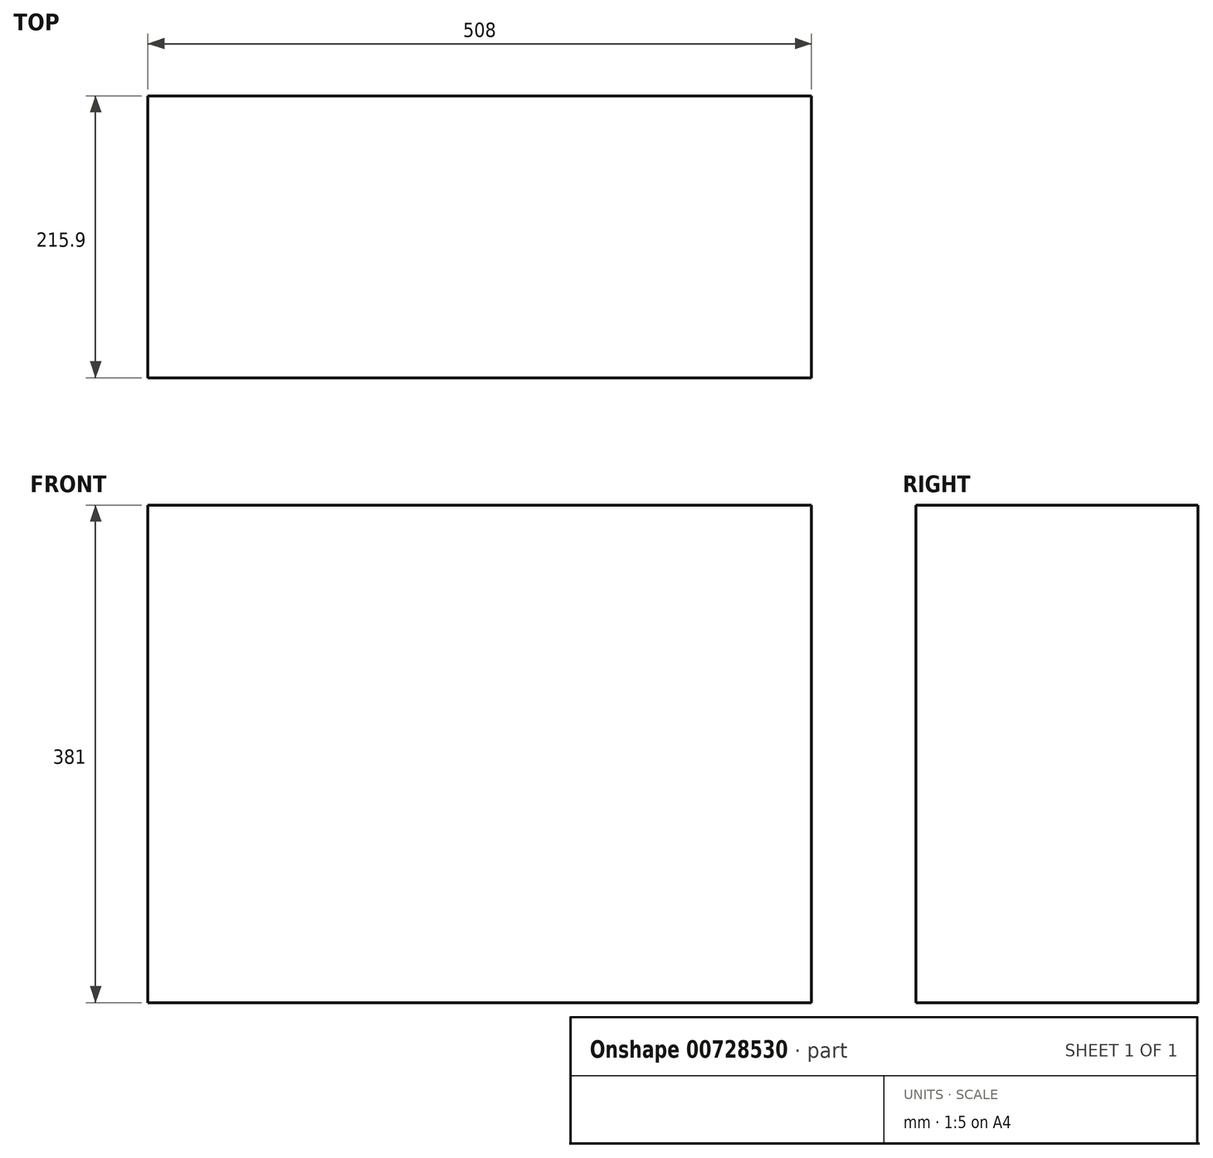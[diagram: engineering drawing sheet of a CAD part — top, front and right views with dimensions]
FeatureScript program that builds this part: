
annotation { "Feature Type Name" : "Feature", "Feature Type Description" : "" }
export const myFeature = defineFeature(function(context is Context, id is Id, definition is map)
    precondition{}
    {
        {
            var Q0;
            Q0=qCreatedBy(makeId("Top.planeOp"),FACE);
            var sketch = newSketch(context, id + "F0", { "sketchPlane" : qUnion([Q0])});
            skLineSegment(sketch, "E0.bottom", {"start": v(254, 107.95) * mm, "end": v(-254, 107.95) * mm});
            skLineSegment(sketch, "E0.top", {"start": v(254, -107.95) * mm, "end": v(-254, -107.95) * mm});
            skLineSegment(sketch, "E0.left", {"start": v(254, 107.95) * mm, "end": v(254, -107.95) * mm});
            skLineSegment(sketch, "E0.right", {"start": v(-254, 107.95) * mm, "end": v(-254, -107.95) * mm});
            skPoint(sketch, "E0.middle", {"position": v(0, 0) * mm});
            skSolve(sketch);
        }
        {
            var Q0;
            Q0 = qSketchRegion(id + "F0", true);
            extrude(context, id + "F1", {"entities" : qUnion([Q0]), "depth" : 381 * mm, "offsetDistance" : 25.4 * mm});
        }
    });
